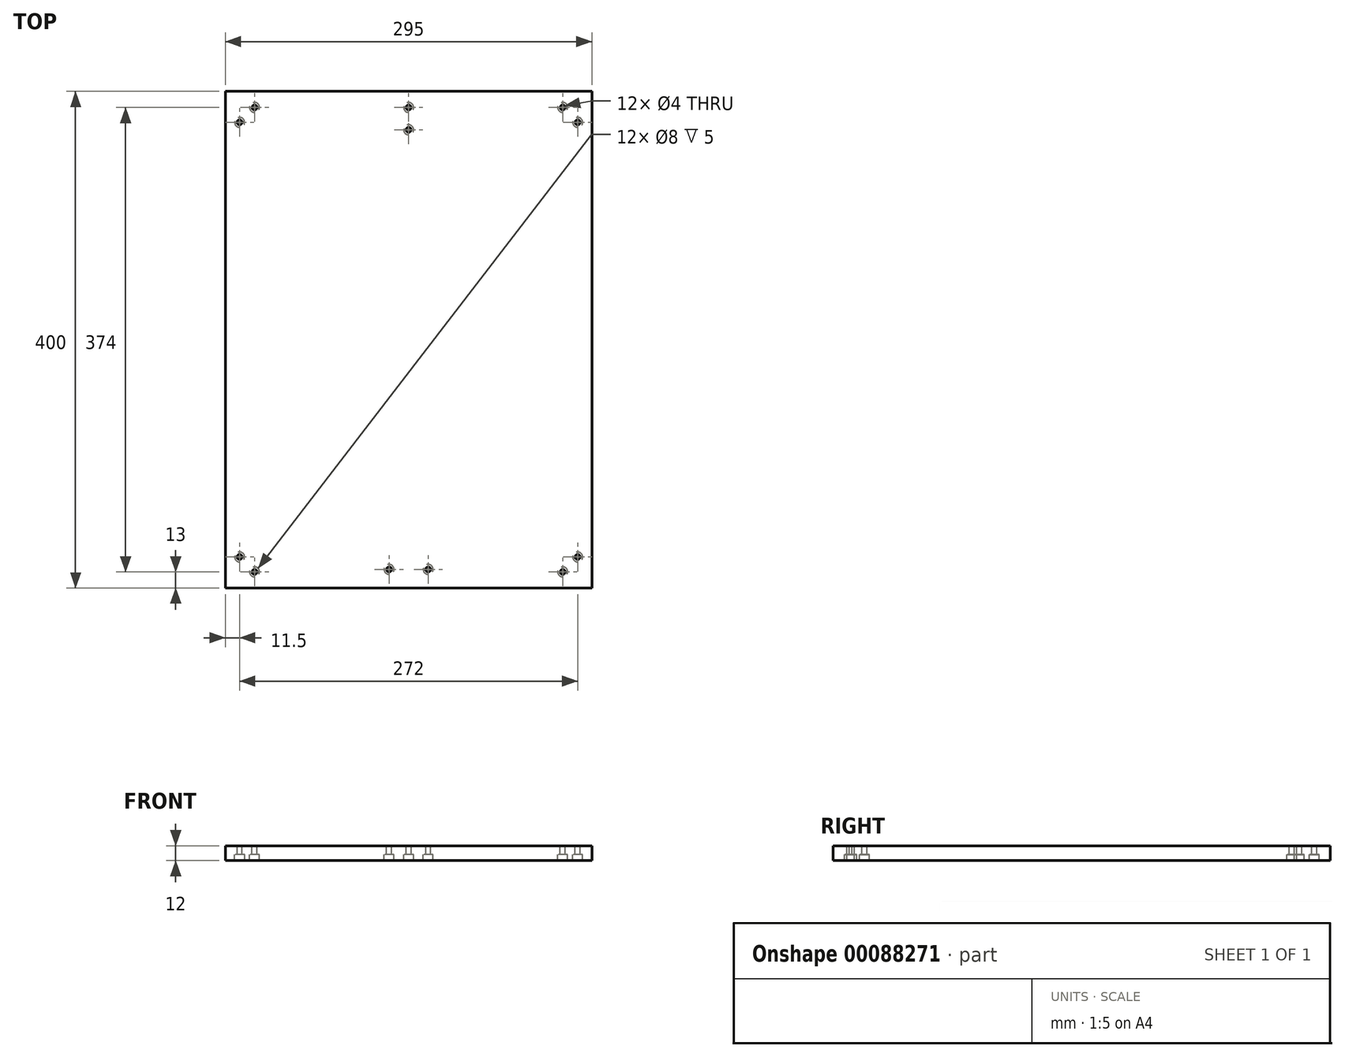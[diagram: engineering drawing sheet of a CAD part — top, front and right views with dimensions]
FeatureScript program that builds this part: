
annotation { "Feature Type Name" : "Feature", "Feature Type Description" : "" }
export const myFeature = defineFeature(function(context is Context, id is Id, definition is map)
    precondition{}
    {
        {
            var Q0;
            Q0=qCreatedBy(makeId("Top.planeOp"),FACE);
            var sketch = newSketch(context, id + "F0", { "sketchPlane" : qUnion([Q0])});
            skLineSegment(sketch, "E0.bottom", {"start": v(147.5, -200) * mm, "end": v(-147.5, -200) * mm});
            skLineSegment(sketch, "E0.top", {"start": v(147.5, 200) * mm, "end": v(-147.5, 200) * mm});
            skLineSegment(sketch, "E0.left", {"start": v(147.5, -200) * mm, "end": v(147.5, 200) * mm});
            skLineSegment(sketch, "E0.right", {"start": v(-147.5, -200) * mm, "end": v(-147.5, 200) * mm});
            skPoint(sketch, "E0.middle", {"position": v(0, 0) * mm});
            skSolve(sketch);
        }
        {
            var Q0;
            Q0=qSketchRegion(id+"F0",true);
            extrude(context, id + "F1", {"entities" : qUnion([Q0]), "depth" : 12 * mm});
        }
        {
            var Q0;
            Q0=qCreatedBy(makeId("Top.planeOp"),FACE);
            var sketch = newSketch(context, id + "F2", { "sketchPlane" : qUnion([Q0])});
            skPoint(sketch, "E1", {"position": v(-124, -187) * mm});
            skPoint(sketch, "E2", {"position": v(-136, -175) * mm});
            skPoint(sketch, "E3", {"position": v(-15.75, -185) * mm});
            skPoint(sketch, "E4", {"position": v(15.75, -185) * mm});
            skPoint(sketch, "E5", {"position": v(136, -175) * mm});
            skPoint(sketch, "E6", {"position": v(124, -187) * mm});
            skPoint(sketch, "E7", {"position": v(136, 175) * mm});
            skPoint(sketch, "E8", {"position": v(124, 187) * mm});
            skPoint(sketch, "E9", {"position": v(-124, 187) * mm});
            skPoint(sketch, "E10", {"position": v(-136, 175) * mm});
            skPoint(sketch, "E11", {"position": v(0, 169) * mm});
            skPoint(sketch, "E12", {"position": v(0, 187) * mm});
            skSolve(sketch);
        }
        {
            var Q0;
            Q0=sQuery(id+"F2.wireOp",VERTEX,"E5");
            var Q1;
            Q1=sQuery(id+"F2.wireOp",VERTEX,"E6");
            var Q2;
            Q2=sQuery(id+"F2.wireOp",VERTEX,"E4");
            var Q3;
            Q3=sQuery(id+"F2.wireOp",VERTEX,"E3");
            var Q4;
            Q4=sQuery(id+"F2.wireOp",VERTEX,"E1");
            var Q5;
            Q5=sQuery(id+"F2.wireOp",VERTEX,"E2");
            var Q6;
            Q6=sQuery(id+"F2.wireOp",VERTEX,"E10");
            var Q7;
            Q7=sQuery(id+"F2.wireOp",VERTEX,"E9");
            var Q8;
            Q8=sQuery(id+"F2.wireOp",VERTEX,"E12");
            var Q9;
            Q9=sQuery(id+"F2.wireOp",VERTEX,"E11");
            var Q10;
            Q10=sQuery(id+"F2.wireOp",VERTEX,"E8");
            var Q11;
            Q11=sQuery(id+"F2.wireOp",VERTEX,"E7");
            var Q12;
            Q12=makeQuery(id+"F1.opExtrude","SWEPT_BODY",BODY,{"disambiguationData":[OSD([sQuery(id+"F0.wireOp",EDGE,"E0.bottom"),sQuery(id+"F0.wireOp",EDGE,"E0.top"),sQuery(id+"F0.wireOp",EDGE,"E0.left"),sQuery(id+"F0.wireOp",EDGE,"E0.right")])]});
            hole(context, id + "F3", {"style" : HoleStyle.C_BORE, "endStyle" : HoleEndStyle.THROUGH, "oppositeDirection" : true, "holeDiameter" : 4 * mm, "cBoreDiameter" : 8 * mm, "cBoreDepth" : 5 * mm, "startFromSketch" : true, "locations" : qUnion([Q0, Q1, Q2, Q3, Q4, Q5, Q6, Q7, Q8, Q9, Q10, Q11]), "scope" : qUnion([Q12]), "isTappedThrough" : true});
        }
    });
